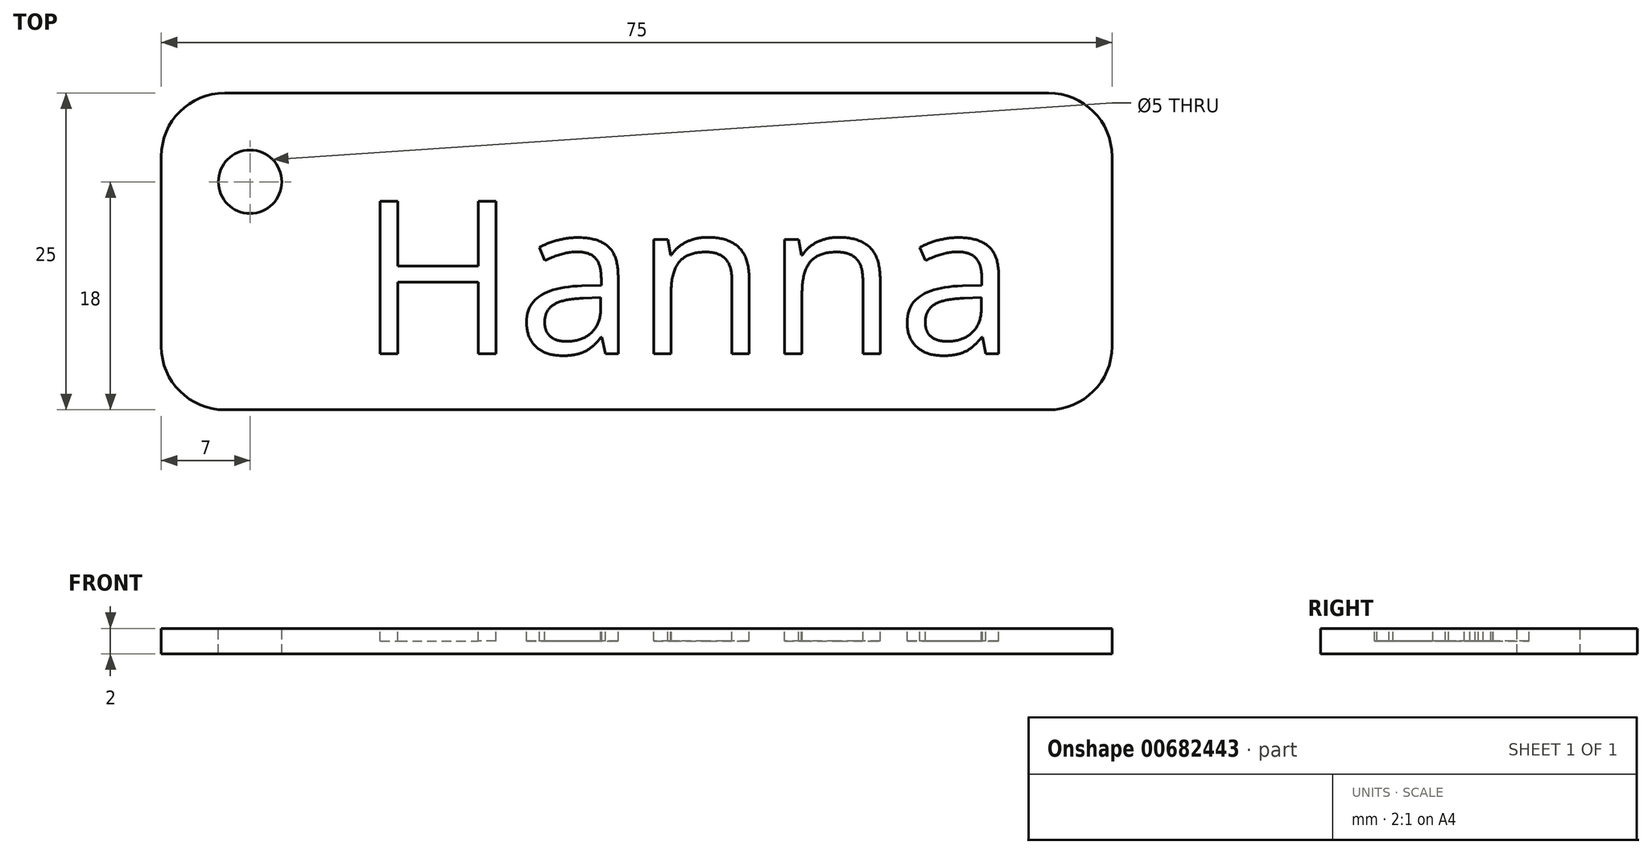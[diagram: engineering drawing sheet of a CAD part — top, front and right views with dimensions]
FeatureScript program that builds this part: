
annotation { "Feature Type Name" : "Feature", "Feature Type Description" : "" }
export const myFeature = defineFeature(function(context is Context, id is Id, definition is map)
    precondition{}
    {
        {
            var Q0;
            Q0=qCreatedBy(makeId("Top.planeOp"),FACE);
            var sketch = newSketch(context, id + "F0", { "sketchPlane" : qUnion([Q0])});
            skLineSegment(sketch, "E0.bottom", {"start": v(-32.5, -12.5) * mm, "end": v(32.5, -12.5) * mm});
            skLineSegment(sketch, "E0.top", {"start": v(-32.5, 12.5) * mm, "end": v(32.5, 12.5) * mm});
            skLineSegment(sketch, "E0.left", {"start": v(-37.5, -7.5) * mm, "end": v(-37.5, 7.5) * mm});
            skLineSegment(sketch, "E0.right", {"start": v(37.5, -7.5) * mm, "end": v(37.5, 7.5) * mm});
            skPoint(sketch, "E0.middle", {"position": v(0, 0) * mm});
            skPoint(sketch, "E1.visualSharp", {"position": v(-37.5, 12.5) * mm});
            skArc(sketch, "E1.filletArc", {"start": v(-32.5, 12.5) * mm, "mid": v(-36.04, 11.04) * mm, "end": v(-37.5, 7.5) * mm});
            skPoint(sketch, "E2.visualSharp", {"position": v(-37.5, -12.5) * mm});
            skArc(sketch, "E2.filletArc", {"start": v(-37.5, -7.5) * mm, "mid": v(-36.04, -11.04) * mm, "end": v(-32.5, -12.5) * mm});
            skPoint(sketch, "E3.visualSharp", {"position": v(37.5, -12.5) * mm});
            skArc(sketch, "E3.filletArc", {"start": v(32.5, -12.5) * mm, "mid": v(36.04, -11.04) * mm, "end": v(37.5, -7.5) * mm});
            skPoint(sketch, "E4.visualSharp", {"position": v(37.5, 12.5) * mm});
            skArc(sketch, "E4.filletArc", {"start": v(37.5, 7.5) * mm, "mid": v(36.04, 11.04) * mm, "end": v(32.5, 12.5) * mm});
            skSolve(sketch);
        }
        {
            var Q0;
            Q0 = qSketchRegion(id + "F0", true);
            extrude(context, id + "F1", {"entities" : qUnion([Q0]), "depth" : 2 * mm, "offsetDistance" : 25.4 * mm});
        }
        {
            var Q0;
            Q0=makeQuery(id+"F1.opExtrude","CAP_FACE",FACE,{"disambiguationData":[OSD([sQuery(id+"F0.wireOp",EDGE,"E0.bottom"),sQuery(id+"F0.wireOp",EDGE,"E0.top"),sQuery(id+"F0.wireOp",EDGE,"E0.left"),sQuery(id+"F0.wireOp",EDGE,"E0.right"),sQuery(id+"F0.wireOp",EDGE,"E1.filletArc"),sQuery(id+"F0.wireOp",EDGE,"E2.filletArc"),sQuery(id+"F0.wireOp",EDGE,"E3.filletArc"),sQuery(id+"F0.wireOp",EDGE,"E4.filletArc")])],"isStart":false});
            var sketch = newSketch(context, id + "F2", { "sketchPlane" : qUnion([Q0])});
            skPoint(sketch, "E5", {"position": v(-30.5, 5.5) * mm});
            skSolve(sketch);
        }
        {
            var Q0;
            Q0=sQuery(id+"F2.wireOp",VERTEX,"E5");
            var Q1;
            Q1=makeQuery(id+"F1.opExtrude","SWEPT_BODY",BODY,{"disambiguationData":[OSD([sQuery(id+"F0.wireOp",EDGE,"E0.bottom"),sQuery(id+"F0.wireOp",EDGE,"E0.top"),sQuery(id+"F0.wireOp",EDGE,"E0.left"),sQuery(id+"F0.wireOp",EDGE,"E0.right"),sQuery(id+"F0.wireOp",EDGE,"E1.filletArc"),sQuery(id+"F0.wireOp",EDGE,"E2.filletArc"),sQuery(id+"F0.wireOp",EDGE,"E3.filletArc"),sQuery(id+"F0.wireOp",EDGE,"E4.filletArc")])]});
            hole(context, id + "F3", {"style" : HoleStyle.SIMPLE, "endStyle" : HoleEndStyle.THROUGH, "holeDiameter" : 5 * mm, "majorDiameter" : 5 * mm, "isTappedThrough" : true, "tappedDepth" : 12 * mm, "tapClearance" : 3, "locations" : qUnion([Q0]), "scope" : qUnion([Q1])});
        }
        {
            var Q0;
            Q0=makeQuery(id+"F1.opExtrude","CAP_FACE",FACE,{"disambiguationData":[OSD([sQuery(id+"F0.wireOp",EDGE,"E0.bottom"),sQuery(id+"F0.wireOp",EDGE,"E0.top"),sQuery(id+"F0.wireOp",EDGE,"E0.left"),sQuery(id+"F0.wireOp",EDGE,"E0.right"),sQuery(id+"F0.wireOp",EDGE,"E1.filletArc"),sQuery(id+"F0.wireOp",EDGE,"E2.filletArc"),sQuery(id+"F0.wireOp",EDGE,"E3.filletArc"),sQuery(id+"F0.wireOp",EDGE,"E4.filletArc")])],"isStart":false});
            var sketch = newSketch(context, id + "F4", { "sketchPlane" : qUnion([Q0])});
            skText(sketch, "E6", { "text": "Hanna", "fontName": "OpenSans-Regular.ttf"});
            const initialGuessF4  = {"E6": [-0.02188, -0.00806, 1, 0, 0.01212]};
            skSetInitialGuess(sketch, initialGuessF4);
            skSolve(sketch);
        }
        {
            var Q0;
            Q0 = qSketchRegion(id + "F4", true);
            extrude(context, id + "F5", {"entities" : qUnion([Q0]), "operationType" : NewBodyOperationType.REMOVE, "oppositeDirection" : true, "depth" : 1 * mm, "offsetDistance" : 25 * mm});
        }
    });
